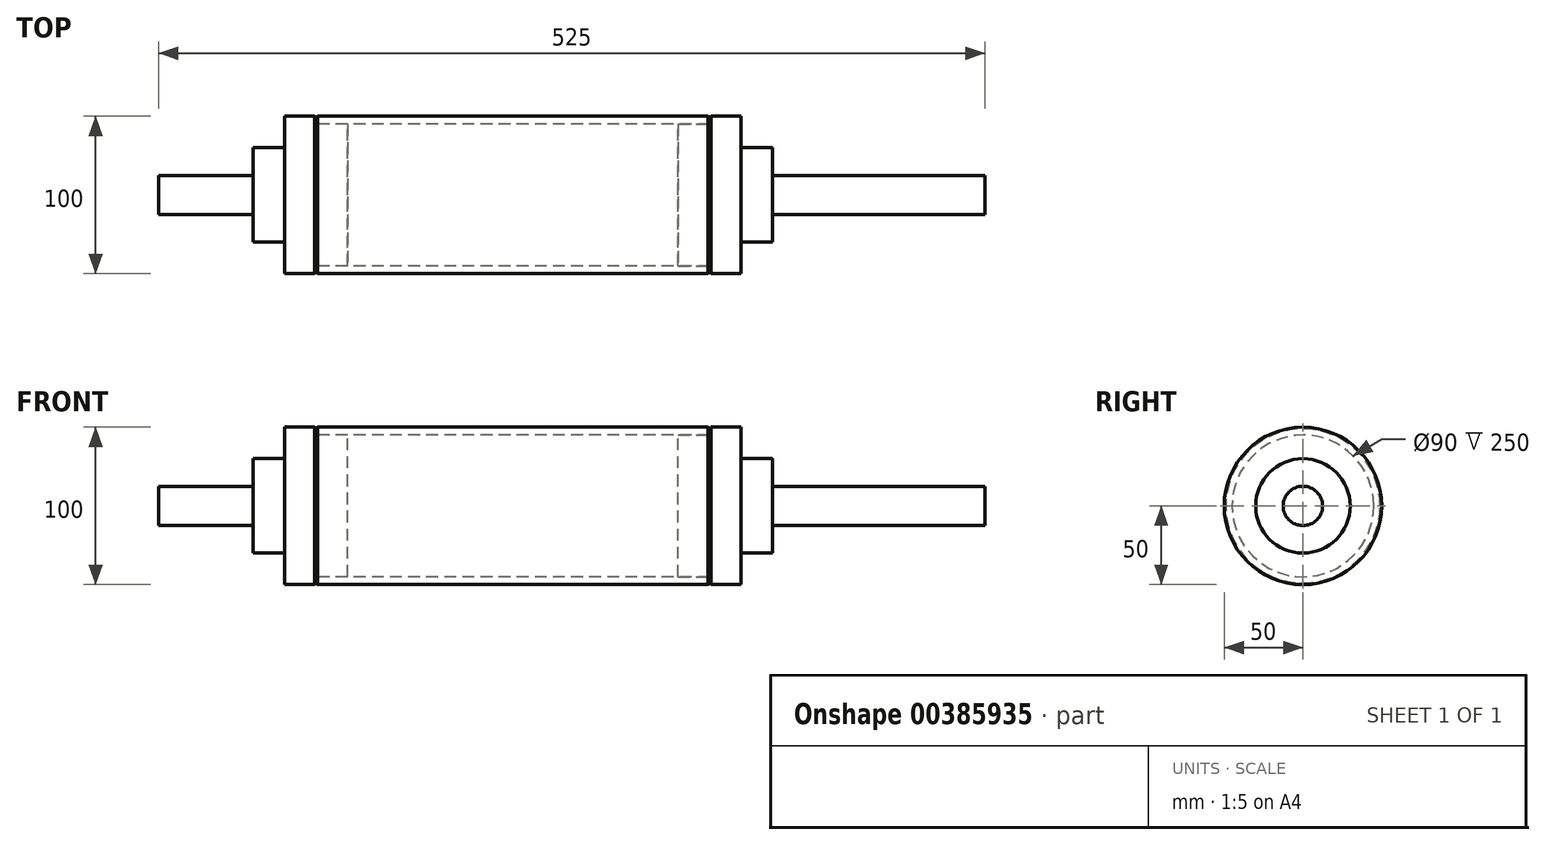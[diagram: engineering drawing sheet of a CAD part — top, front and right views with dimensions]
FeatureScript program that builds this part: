
annotation { "Feature Type Name" : "Feature", "Feature Type Description" : "" }
export const myFeature = defineFeature(function(context is Context, id is Id, definition is map)
    precondition{}
    {
        {
            var Q0;
            Q0=qCreatedBy(makeId("Front.planeOp"),FACE);
            var sketch = newSketch(context, id + "F0", { "sketchPlane" : qUnion([Q0])});
            skLineSegment(sketch, "E0", {"start": v(0, 45) * mm, "end": v(0, 50) * mm});
            skLineSegment(sketch, "E1", {"start": v(0, 50) * mm, "end": v(125, 50) * mm});
            skLineSegment(sketch, "E2", {"start": v(125, 50) * mm, "end": v(125, 45) * mm});
            skLineSegment(sketch, "E3", {"start": v(125, 0) * mm, "end": v(0, 0) * mm});
            skLineSegment(sketch, "E4", {"start": v(125, 50) * mm, "end": v(145, 50) * mm});
            skLineSegment(sketch, "E5", {"start": v(145, 50) * mm, "end": v(145, 0) * mm});
            skLineSegment(sketch, "E6", {"start": v(145, 0) * mm, "end": v(105, 0) * mm});
            skLineSegment(sketch, "E7", {"start": v(105, 0) * mm, "end": v(105, 45) * mm});
            skLineSegment(sketch, "E8", {"start": v(105, 45) * mm, "end": v(125, 45) * mm});
            skLineSegment(sketch, "E9", {"start": v(0, 45) * mm, "end": v(105, 45) * mm});
            skLineSegment(sketch, "E10", {"start": v(145, 30) * mm, "end": v(165, 30) * mm});
            skLineSegment(sketch, "E11", {"start": v(165, 30) * mm, "end": v(165, 0) * mm});
            skLineSegment(sketch, "E12", {"start": v(165, 0) * mm, "end": v(145, 0) * mm});
            skLineSegment(sketch, "E13", {"start": v(165, 12.5) * mm, "end": v(175, 12.5) * mm});
            skLineSegment(sketch, "E14", {"start": v(175, 12.5) * mm, "end": v(175, 0) * mm});
            skLineSegment(sketch, "E15", {"start": v(175, 0) * mm, "end": v(165, 0) * mm});
            skLineSegment(sketch, "E16", {"start": v(175, 12.5) * mm, "end": v(225, 12.5) * mm});
            skLineSegment(sketch, "E17", {"start": v(225, 12.5) * mm, "end": v(225, 0) * mm});
            skLineSegment(sketch, "E18", {"start": v(225, 0) * mm, "end": v(175, 0) * mm});
            skLineSegment(sketch, "E19.MirrorCS", {"start": v(0, 50) * mm, "end": v(-125, 50) * mm});
            skLineSegment(sketch, "E20.MirrorCS", {"start": v(0, 45) * mm, "end": v(-105, 45) * mm});
            skLineSegment(sketch, "E21.MirrorCS", {"start": v(-105, 0) * mm, "end": v(-105, 45) * mm});
            skLineSegment(sketch, "E22.MirrorCS", {"start": v(-105, 45) * mm, "end": v(-125, 45) * mm});
            skLineSegment(sketch, "E23.MirrorCS", {"start": v(-125, 50) * mm, "end": v(-125, 45) * mm});
            skLineSegment(sketch, "E24.MirrorCS", {"start": v(-125, 50) * mm, "end": v(-145, 50) * mm});
            skLineSegment(sketch, "E25.MirrorCS", {"start": v(-145, 0) * mm, "end": v(-105, 0) * mm});
            skLineSegment(sketch, "E26.MirrorCS", {"start": v(-125, 0) * mm, "end": v(0, 0) * mm});
            skLineSegment(sketch, "E27.MirrorCS", {"start": v(-145, 50) * mm, "end": v(-145, 0) * mm});
            skLineSegment(sketch, "E28.MirrorCS", {"start": v(-145, 30) * mm, "end": v(-165, 30) * mm});
            skLineSegment(sketch, "E29.MirrorCS", {"start": v(-165, 0) * mm, "end": v(-145, 0) * mm});
            skLineSegment(sketch, "E30.MirrorCS", {"start": v(-165, 30) * mm, "end": v(-165, 0) * mm});
            skLineSegment(sketch, "E31.MirrorCS", {"start": v(-165, 12.5) * mm, "end": v(-175, 12.5) * mm});
            skLineSegment(sketch, "E32.MirrorCS", {"start": v(-175, 12.5) * mm, "end": v(-175, 0) * mm});
            skLineSegment(sketch, "E33.MirrorCS", {"start": v(-175, 12.5) * mm, "end": v(-225, 12.5) * mm});
            skLineSegment(sketch, "E34.MirrorCS", {"start": v(-225, 12.5) * mm, "end": v(-225, 0) * mm});
            skLineSegment(sketch, "E35.MirrorCS", {"start": v(-225, 0) * mm, "end": v(-175, 0) * mm});
            skLineSegment(sketch, "E36.MirrorCS", {"start": v(-175, 0) * mm, "end": v(-165, 0) * mm});
            skSolve(sketch);
        }
        {
            var Q0;
            Q0=makeQuery(id+"F0.imprint","IMPRINT",FACE,{"disambiguationData":[TD([[makeQuery(id+"F0.imprint","IMPRINT",EDGE,{"derivedFrom":sQuery(id+"F0.wireOp",EDGE,"E0")}),1.0]])]});
            var Q1;
            Q1=makeQuery(id+"F0.imprint","IMPRINT",FACE,{"disambiguationData":[TD([[makeQuery(id+"F0.imprint","IMPRINT",EDGE,{"derivedFrom":sQuery(id+"F0.wireOp",EDGE,"E0")}),-1.0]])]});
            var Q2;
            Q2=sQuery(id+"F0.wireOp",EDGE,"E26.MirrorCS");
            revolve(context, id + "F1", {"entities" : qUnion([Q0, Q1]), "axis" : qUnion([Q2]), "revolveType" : RevolveType.FULL});
        }
        {
            var Q0;
            Q0=makeQuery(id+"F0.imprint","IMPRINT",FACE,{"disambiguationData":[TD([[makeQuery(id+"F0.imprint","IMPRINT",EDGE,{"derivedFrom":sQuery(id+"F0.wireOp",EDGE,"E2")}),1.0]])]});
            var Q1;
            Q1=sQuery(id+"F0.wireOp",EDGE,"E6");
            revolve(context, id + "F2", {"entities" : qUnion([Q0]), "axis" : qUnion([Q1]), "revolveType" : RevolveType.FULL});
        }
        {
            var Q0;
            {var subQ3=sQuery(id+"F0.wireOp",EDGE,"E10");Q0=makeQuery(id+"F0.imprint","IMPRINT",FACE,{"disambiguationData":[TD([[makeQuery(id+"F0.imprint","IMPRINT",EDGE,{"derivedFrom":subQ3}),-1.0]])]});}
            var Q1;
            {var subQ2=sQuery(id+"F0.wireOp",EDGE,"E13");Q1=makeQuery(id+"F0.imprint","IMPRINT",FACE,{"disambiguationData":[TD([[makeQuery(id+"F0.imprint","IMPRINT",EDGE,{"derivedFrom":subQ2}),-1.0]])]});}
            var Q2;
            Q2=makeQuery(id+"F0.imprint","IMPRINT",FACE,{"disambiguationData":[TD([[makeQuery(id+"F0.imprint","IMPRINT",EDGE,{"derivedFrom":sQuery(id+"F0.wireOp",EDGE,"E14")}),1.0]])]});
            var Q3;
            Q3=sQuery(id+"F0.wireOp",EDGE,"E12");
            revolve(context, id + "F3", {"operationType" : NewBodyOperationType.ADD, "entities" : qUnion([Q0, Q1, Q2]), "axis" : qUnion([Q3]), "revolveType" : RevolveType.FULL});
        }
        {
            var Q0;
            Q0=makeQuery(id+"F2.opRevolve","SWEPT_EDGE",EDGE,{"disambiguationData":[OSD([sQuery(id+"F0.wireOp",EDGE,"E1"),sQuery(id+"F0.wireOp",EDGE,"E2"),sQuery(id+"F0.wireOp",EDGE,"E4")])]});
            chamfer(context, id + "F4", {"entities" : qUnion([Q0]), "chamferType" : ChamferType.OFFSET_ANGLE, "width" : 1 * mm, "oppositeDirection" : false, "angle" : 45 * degree, "tangentPropagation" : true});
        }
        {
            var Q0;
            Q0=makeQuery(id+"F1.opRevolve","SWEPT_EDGE",EDGE,{"disambiguationData":[OSD([sQuery(id+"F0.wireOp",EDGE,"E1"),sQuery(id+"F0.wireOp",EDGE,"E2"),sQuery(id+"F0.wireOp",EDGE,"E4")])]});
            chamfer(context, id + "F5", {"entities" : qUnion([Q0]), "chamferType" : ChamferType.OFFSET_ANGLE, "width" : 1 * mm, "oppositeDirection" : false, "angle" : 45 * degree, "tangentPropagation" : true});
        }
        {
            var Q0;
            Q0=makeQuery(id+"F1.opRevolve","SWEPT_EDGE",EDGE,{"disambiguationData":[OSD([sQuery(id+"F0.wireOp",EDGE,"E19.MirrorCS"),sQuery(id+"F0.wireOp",EDGE,"E23.MirrorCS"),sQuery(id+"F0.wireOp",EDGE,"E24.MirrorCS")])]});
            chamfer(context, id + "F6", {"entities" : qUnion([Q0]), "chamferType" : ChamferType.OFFSET_ANGLE, "width" : 1 * mm, "oppositeDirection" : false, "angle" : 45 * degree, "tangentPropagation" : true});
        }
        {
            var Q0;
            Q0=makeQuery(id+"F2.opRevolve","SWEPT_BODY",BODY,{"disambiguationData":[OSD([sQuery(id+"F0.wireOp",EDGE,"E2"),sQuery(id+"F0.wireOp",EDGE,"E4"),sQuery(id+"F0.wireOp",EDGE,"E5"),sQuery(id+"F0.wireOp",EDGE,"E6"),sQuery(id+"F0.wireOp",EDGE,"E7"),sQuery(id+"F0.wireOp",EDGE,"E8")])]});
            var Q1;
            Q1=qCreatedBy(makeId("Right.planeOp"),FACE);
            mirror(context, id + "F7", {"entities" : qUnion([Q0]), "mirrorPlane" : qUnion([Q1])});
        }
        {
            var Q0;
            Q0=makeQuery(id+"F3.opRevolve","SWEPT_FACE",FACE,{"disambiguationData":[OSD([sQuery(id+"F0.wireOp",EDGE,"E17")])]});
            var sketch = newSketch(context, id + "F8", { "sketchPlane" : qUnion([Q0])});
            skCircle(sketch, "E37.0.0", {"center": v(0, 0) * mm, "radius": 12.5 * mm});
            skSolve(sketch);
        }
        {
            var Q0;
            Q0 = qSketchRegion(id + "F8", true);
            extrude(context, id + "F9", {"entities" : qUnion([Q0]), "operationType" : NewBodyOperationType.ADD, "depth" : 75 * mm});
        }
    });
